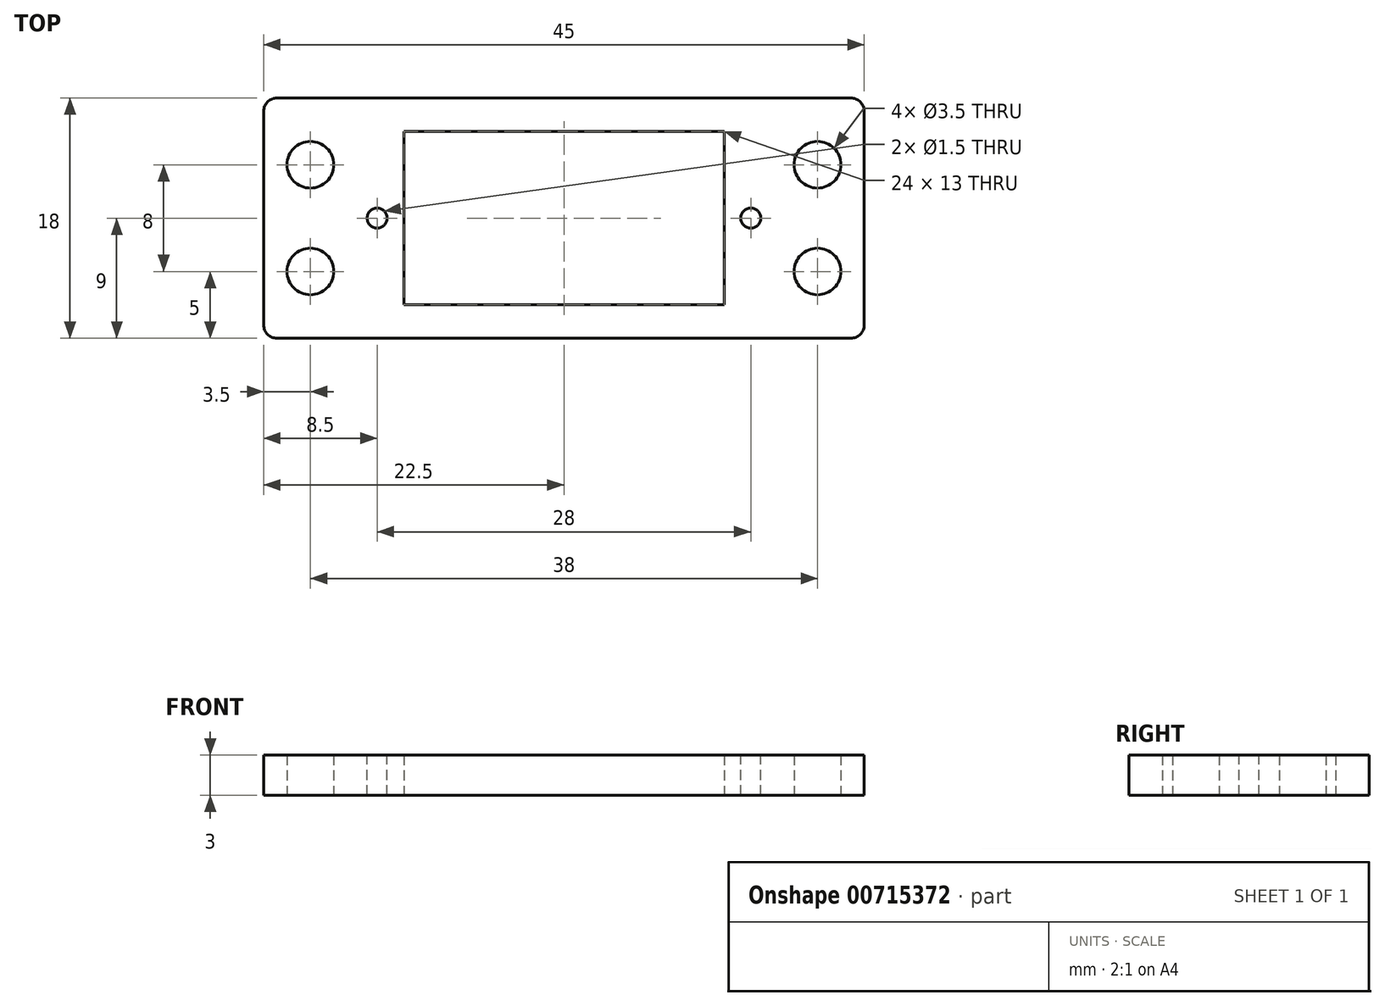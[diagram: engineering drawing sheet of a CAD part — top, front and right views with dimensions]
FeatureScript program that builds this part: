
annotation { "Feature Type Name" : "Feature", "Feature Type Description" : "" }
export const myFeature = defineFeature(function(context is Context, id is Id, definition is map)
    precondition{}
    {
        {
            var Q0;
            Q0=qCreatedBy(makeId("Top.planeOp"),FACE);
            var sketch = newSketch(context, id + "F0", { "sketchPlane" : qUnion([Q0])});
            skLineSegment(sketch, "E0.bottom", {"start": v(19, -4) * mm, "end": v(-19, -4) * mm});
            skLineSegment(sketch, "E0.top", {"start": v(19, 4) * mm, "end": v(-19, 4) * mm});
            skLineSegment(sketch, "E0.left", {"start": v(19, -4) * mm, "end": v(19, 4) * mm});
            skLineSegment(sketch, "E0.right", {"start": v(-19, -4) * mm, "end": v(-19, 4) * mm});
            skPoint(sketch, "E0.middle", {"position": v(0, 0) * mm});
            skLineSegment(sketch, "E1.bottom", {"start": v(-22.5, 9) * mm, "end": v(22.5, 9) * mm});
            skLineSegment(sketch, "E1.top", {"start": v(-22.5, -9) * mm, "end": v(22.5, -9) * mm});
            skLineSegment(sketch, "E1.left", {"start": v(-22.5, 9) * mm, "end": v(-22.5, -9) * mm});
            skLineSegment(sketch, "E1.right", {"start": v(22.5, 9) * mm, "end": v(22.5, -9) * mm});
            skLineSegment(sketch, "E2.bottom", {"start": v(-12, 6.5) * mm, "end": v(12, 6.5) * mm});
            skLineSegment(sketch, "E2.top", {"start": v(-12, -6.5) * mm, "end": v(12, -6.5) * mm});
            skLineSegment(sketch, "E2.left", {"start": v(-12, 6.5) * mm, "end": v(-12, -6.5) * mm});
            skLineSegment(sketch, "E2.right", {"start": v(12, 6.5) * mm, "end": v(12, -6.5) * mm});
            skSolve(sketch);
        }
        {
            var Q0;
            {var subQ1=sQuery(id+"F0.wireOp",EDGE,"E0.left");Q0=makeQuery(id+"F0.imprint","IMPRINT",FACE,{"disambiguationData":[TD([[makeQuery(id+"F0.imprint","IMPRINT",EDGE,{"derivedFrom":subQ1}),-1.0]])]});}
            var Q1;
            {var subQ0=sQuery(id+"F0.wireOp",EDGE,"E0.left");Q1=makeQuery(id+"F0.imprint","IMPRINT",FACE,{"disambiguationData":[TD([[makeQuery(id+"F0.imprint","IMPRINT",EDGE,{"derivedFrom":subQ0}),1.0]])]});}
            var Q2;
            {var subQ0=sQuery(id+"F0.wireOp",EDGE,"E0.right");Q2=makeQuery(id+"F0.imprint","IMPRINT",FACE,{"disambiguationData":[TD([[makeQuery(id+"F0.imprint","IMPRINT",EDGE,{"derivedFrom":subQ0}),-1.0]])]});}
            extrude(context, id + "F1", {"entities" : qUnion([Q0, Q1, Q2]), "depth" : 3 * mm, "offsetDistance" : 25 * mm});
        }
        {
            var Q0;
            Q0=sQuery(id+"F0.wireOp",VERTEX,"E0.right.end");
            var Q1;
            Q1=sQuery(id+"F0.wireOp",VERTEX,"E0.right.start");
            var Q2;
            Q2=sQuery(id+"F0.wireOp",VERTEX,"E0.left.start");
            var Q3;
            Q3=sQuery(id+"F0.wireOp",VERTEX,"E0.left.end");
            var Q4;
            Q4=makeQuery(id+"F1.opExtrude","SWEPT_BODY",BODY,{"disambiguationData":[OSD([sQuery(id+"F0.wireOp",EDGE,"E1.bottom"),sQuery(id+"F0.wireOp",EDGE,"E1.top"),sQuery(id+"F0.wireOp",EDGE,"E1.left"),sQuery(id+"F0.wireOp",EDGE,"E1.right"),sQuery(id+"F0.wireOp",EDGE,"E2.bottom"),sQuery(id+"F0.wireOp",EDGE,"E2.top"),sQuery(id+"F0.wireOp",EDGE,"E2.left"),sQuery(id+"F0.wireOp",EDGE,"E2.right")])]});
            hole(context, id + "F2", {"style" : HoleStyle.SIMPLE, "endStyle" : HoleEndStyle.THROUGH, "oppositeDirection" : true, "holeDiameter" : 3.5 * mm, "majorDiameter" : 5 * mm, "isTappedThrough" : true, "tappedDepth" : 12 * mm, "tapClearance" : 3, "locations" : qUnion([Q0, Q1, Q2, Q3]), "scope" : qUnion([Q4])});
        }
        {
            var Q0;
            Q0=makeQuery(id+"F1.opExtrude","SWEPT_EDGE",EDGE,{"disambiguationData":[OSD([sQuery(id+"F0.wireOp",EDGE,"E1.bottom"),sQuery(id+"F0.wireOp",EDGE,"E1.right")])]});
            var Q1;
            Q1=makeQuery(id+"F1.opExtrude","SWEPT_EDGE",EDGE,{"disambiguationData":[OSD([sQuery(id+"F0.wireOp",EDGE,"E1.top"),sQuery(id+"F0.wireOp",EDGE,"E1.right")])]});
            var Q2;
            Q2=makeQuery(id+"F1.opExtrude","SWEPT_EDGE",EDGE,{"disambiguationData":[OSD([sQuery(id+"F0.wireOp",EDGE,"E1.top"),sQuery(id+"F0.wireOp",EDGE,"E1.left")])]});
            var Q3;
            Q3=makeQuery(id+"F1.opExtrude","SWEPT_EDGE",EDGE,{"disambiguationData":[OSD([sQuery(id+"F0.wireOp",EDGE,"E1.bottom"),sQuery(id+"F0.wireOp",EDGE,"E1.left")])]});
            fillet(context, id + "F3", {"entities" : qUnion([Q0, Q1, Q2, Q3]), "radius" : 1 * mm, "tangentPropagation" : true, "allowEdgeOverflow" : false});
        }
        {
            var Q0;
            Q0=makeQuery(id+"F1.opExtrude","CAP_FACE",FACE,{"disambiguationData":[OSD([sQuery(id+"F0.wireOp",EDGE,"E1.bottom"),sQuery(id+"F0.wireOp",EDGE,"E1.top"),sQuery(id+"F0.wireOp",EDGE,"E1.left"),sQuery(id+"F0.wireOp",EDGE,"E1.right"),sQuery(id+"F0.wireOp",EDGE,"E2.bottom"),sQuery(id+"F0.wireOp",EDGE,"E2.top"),sQuery(id+"F0.wireOp",EDGE,"E2.left"),sQuery(id+"F0.wireOp",EDGE,"E2.right")])],"isStart":false});
            var sketch = newSketch(context, id + "F4", { "sketchPlane" : qUnion([Q0])});
            skLineSegment(sketch, "E3", {"start": v(0, 0) * mm, "end": v(-14, 0) * mm});
            skLineSegment(sketch, "E4", {"start": v(0, 0) * mm, "end": v(14, 0) * mm});
            skSolve(sketch);
        }
        {
            var Q0;
            Q0=sQuery(id+"F4.wireOp",VERTEX,"E3.end");
            var Q1;
            Q1=sQuery(id+"F4.wireOp",VERTEX,"E4.end");
            var Q2;
            Q2=makeQuery(id+"F1.opExtrude","SWEPT_BODY",BODY,{"disambiguationData":[OSD([sQuery(id+"F0.wireOp",EDGE,"E1.bottom"),sQuery(id+"F0.wireOp",EDGE,"E1.top"),sQuery(id+"F0.wireOp",EDGE,"E1.left"),sQuery(id+"F0.wireOp",EDGE,"E1.right"),sQuery(id+"F0.wireOp",EDGE,"E2.bottom"),sQuery(id+"F0.wireOp",EDGE,"E2.top"),sQuery(id+"F0.wireOp",EDGE,"E2.left"),sQuery(id+"F0.wireOp",EDGE,"E2.right")])]});
            hole(context, id + "F5", {"style" : HoleStyle.SIMPLE, "endStyle" : HoleEndStyle.THROUGH, "holeDiameter" : 1.5 * mm, "majorDiameter" : 5 * mm, "isTappedThrough" : true, "tappedDepth" : 12 * mm, "tapClearance" : 3, "locations" : qUnion([Q0, Q1]), "scope" : qUnion([Q2])});
        }
    });
